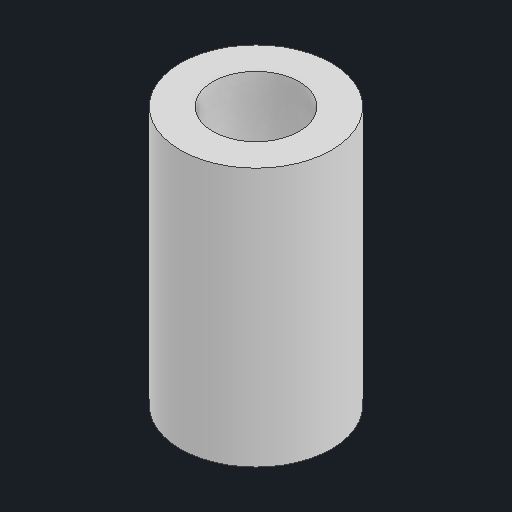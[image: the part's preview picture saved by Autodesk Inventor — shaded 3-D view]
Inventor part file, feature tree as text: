
AUTODESK INVENTOR PART (.ipt)
format: ipt  version: 2024 (Build 280153000, 153)  size: 174,080 bytes
history: native  units: in
note: dims shown in document units (in); Inventor stores cm internally (conversion verified against a paired STEP export)
features: extrude x1, sketch x1
ambient origin geometry x8: Origin, YZ Plane, XZ Plane, XY Plane, X Axis, Y Axis, Z Axis, Center Point
bodies: Solid1 (feature_tree)
feature tree (2):
  extrude  "Extrusion1"  Depth=0.4724in
  sketch  "Sketch1"  dims[d0=0.1575in d1=0.2756in d2=0.4724in d3=0.0in]
